AUTODESK INVENTOR PART (.ipt)
format: ipt  version: 2021 (Build 250183000, 183)  size: 90,112 bytes
history: native  units: mm
features: extrude x3, sketch x3
ambient origin geometry x8: Origin, YZ Plane, XZ Plane, XY Plane, X Axis, Y Axis, Z Axis, Center Point
bodies: Solid1 (feature_tree)
feature tree (6):
  extrude  "Extrusion1"  Depth=1.0mm TaperAngle=0.0deg
  extrude  "Extrusion2"  Depth=12.0mm TaperAngle=0.0deg
  extrude  "Extrusion3"  Depth=0.3mm TaperAngle=0.0deg
  sketch  "Sketch1"  dims[d0=3.0mm d1=1.0mm d2=0.0mm]
  sketch  "Sketch2"  dims[d3=1.5mm d4=12.0mm d5=0.0mm]
  sketch  "Sketch3"  dims[d6=0.5mm d7=0.3mm d8=0.0mm]
